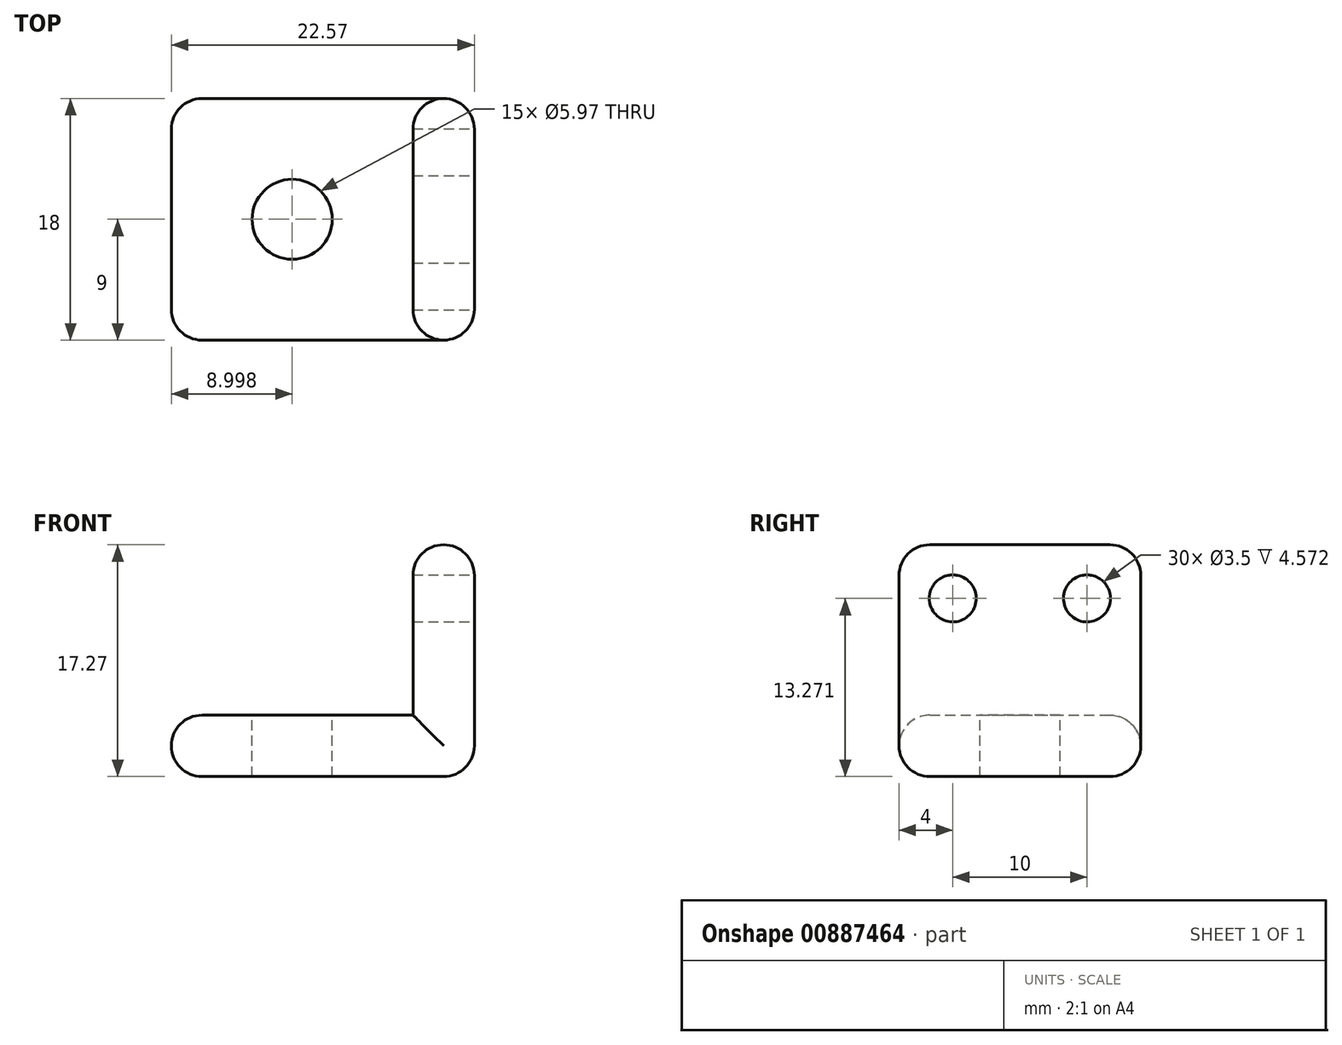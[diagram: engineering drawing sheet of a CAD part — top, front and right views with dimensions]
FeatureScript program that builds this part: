
annotation { "Feature Type Name" : "Feature", "Feature Type Description" : "" }
export const myFeature = defineFeature(function(context is Context, id is Id, definition is map)
    precondition{}
    {
        {
            var Q0;
            Q0=qCreatedBy(makeId("Front.planeOp"),FACE);
            var sketch = newSketch(context, id + "F0", { "sketchPlane" : qUnion([Q0])});
            skLineSegment(sketch, "E0.bottom", {"start": v(-12.02, -3.56) * mm, "end": v(5.98, -3.56) * mm});
            skLineSegment(sketch, "E0.top", {"start": v(-12.02, -8.13) * mm, "end": v(5.98, -8.13) * mm});
            skLineSegment(sketch, "E0.left", {"start": v(-12.02, -3.56) * mm, "end": v(-12.02, -8.13) * mm});
            skLineSegment(sketch, "E0.right", {"start": v(5.98, -3.56) * mm, "end": v(5.98, -8.13) * mm});
            skLineSegment(sketch, "E1.bottom", {"start": v(5.98, -8.13) * mm, "end": v(10.55, -8.13) * mm});
            skLineSegment(sketch, "E1.top", {"start": v(5.98, 9.14) * mm, "end": v(10.55, 9.14) * mm});
            skLineSegment(sketch, "E1.left", {"start": v(5.98, -8.13) * mm, "end": v(5.98, 9.14) * mm});
            skLineSegment(sketch, "E1.right", {"start": v(10.55, -8.13) * mm, "end": v(10.55, 9.14) * mm});
            skSolve(sketch);
        }
        {
            var Q0;
            {var subQ3=sQuery(id+"F0.wireOp",EDGE,"E1.bottom");Q0=makeQuery(id+"F0.imprint","IMPRINT",FACE,{"disambiguationData":[TD([[makeQuery(id+"F0.imprint","IMPRINT",EDGE,{"derivedFrom":subQ3}),1.0]])]});}
            var Q1;
            {var subQ0=sQuery(id+"F0.wireOp",EDGE,"E0.bottom");Q1=makeQuery(id+"F0.imprint","IMPRINT",FACE,{"disambiguationData":[TD([[makeQuery(id+"F0.imprint","IMPRINT",EDGE,{"derivedFrom":subQ0}),-1.0]])]});}
            extrude(context, id + "F1", {"entities" : qUnion([Q0, Q1]), "depth" : 18 * mm, "offsetDistance" : 25.4 * mm});
        }
        {
            var Q0;
            Q0=makeQuery(id+"F1.opExtrude","SWEPT_FACE",FACE,{"disambiguationData":[OSD([sQuery(id+"F0.wireOp",EDGE,"E0.bottom")])]});
            var sketch = newSketch(context, id + "F2", { "sketchPlane" : qUnion([Q0])});
            skCircle(sketch, "E2", {"center": v(-3.02, -9) * mm, "radius": 2.98 * mm});
            skPoint(sketch, "E2.centerSnap0", {"position": v(-12.02, -9) * mm});
            skSolve(sketch);
        }
        {
            var Q0;
            Q0=makeQuery(id+"F2.imprint","IMPRINT",FACE,{"disambiguationData":[TD([[makeQuery(id+"F2.imprint","IMPRINT",EDGE,{"derivedFrom":sQuery(id+"F2.wireOp",EDGE,"E2")}),1.0]])]});
            extrude(context, id + "F3", {"entities" : qUnion([Q0]), "operationType" : NewBodyOperationType.REMOVE, "oppositeDirection" : true, "depth" : 25.4 * mm, "offsetDistance" : 25.4 * mm});
        }
        {
            var Q0;
            Q0=makeQuery(id+"F1.opExtrude","SWEPT_FACE",FACE,{"disambiguationData":[OSD([sQuery(id+"F0.wireOp",EDGE,"E1.right")])]});
            var sketch = newSketch(context, id + "F4", { "sketchPlane" : qUnion([Q0])});
            skCircle(sketch, "E3", {"center": v(-14, 5.14) * mm, "radius": 1.75 * mm});
            skCircle(sketch, "E4", {"center": v(-4, 5.14) * mm, "radius": 1.75 * mm});
            skSolve(sketch);
        }
        {
            var Q0;
            Q0=makeQuery(id+"F4.imprint","IMPRINT",FACE,{"disambiguationData":[TD([[makeQuery(id+"F4.imprint","IMPRINT",EDGE,{"derivedFrom":sQuery(id+"F4.wireOp",EDGE,"E3")}),1.0]])]});
            var Q1;
            Q1=makeQuery(id+"F4.imprint","IMPRINT",FACE,{"disambiguationData":[TD([[makeQuery(id+"F4.imprint","IMPRINT",EDGE,{"derivedFrom":sQuery(id+"F4.wireOp",EDGE,"E4")}),1.0]])]});
            extrude(context, id + "F5", {"entities" : qUnion([Q0, Q1]), "operationType" : NewBodyOperationType.REMOVE, "oppositeDirection" : true, "depth" : 25.4 * mm, "offsetDistance" : 25.4 * mm});
        }
        {
            var Q0;
            Q0=makeQuery(id+"F1.opExtrude","CAP_EDGE",EDGE,{"disambiguationData":[OSD([sQuery(id+"F0.wireOp",EDGE,"E1.top")])],"isStart":false});
            var Q1;
            Q1=makeQuery(id+"F1.opExtrude","CAP_EDGE",EDGE,{"disambiguationData":[OSD([sQuery(id+"F0.wireOp",EDGE,"E1.top")])],"isStart":true});
            var Q2;
            Q2=makeQuery(id+"F1.opExtrude","CAP_EDGE",EDGE,{"disambiguationData":[OSD([sQuery(id+"F0.wireOp",EDGE,"E0.left")])],"isStart":false});
            var Q3;
            Q3=makeQuery(id+"F1.opExtrude","CAP_EDGE",EDGE,{"disambiguationData":[OSD([sQuery(id+"F0.wireOp",EDGE,"E0.left")])],"isStart":true});
            var Q4;
            Q4=makeQuery(id+"F1.opExtrude","CAP_FACE",FACE,{"disambiguationData":[OSD([sQuery(id+"F0.wireOp",EDGE,"E0.bottom"),sQuery(id+"F0.wireOp",EDGE,"E0.top"),sQuery(id+"F0.wireOp",EDGE,"E0.left"),sQuery(id+"F0.wireOp",EDGE,"E1.bottom"),sQuery(id+"F0.wireOp",EDGE,"E1.top"),sQuery(id+"F0.wireOp",EDGE,"E1.left"),sQuery(id+"F0.wireOp",EDGE,"E1.right")])],"isStart":false});
            var Q5;
            Q5=makeQuery(id+"F1.opExtrude","CAP_FACE",FACE,{"disambiguationData":[OSD([sQuery(id+"F0.wireOp",EDGE,"E0.bottom"),sQuery(id+"F0.wireOp",EDGE,"E0.top"),sQuery(id+"F0.wireOp",EDGE,"E0.left"),sQuery(id+"F0.wireOp",EDGE,"E1.bottom"),sQuery(id+"F0.wireOp",EDGE,"E1.top"),sQuery(id+"F0.wireOp",EDGE,"E1.left"),sQuery(id+"F0.wireOp",EDGE,"E1.right")])],"isStart":true});
            var Q6;
            Q6=makeQuery(id+"F1.opExtrude","SWEPT_FACE",FACE,{"disambiguationData":[OSD([sQuery(id+"F0.wireOp",EDGE,"E0.left")])]});
            var Q7;
            Q7=makeQuery(id+"F1.opExtrude","SWEPT_EDGE",EDGE,{"disambiguationData":[OSD([sQuery(id+"F0.wireOp",EDGE,"E1.bottom"),sQuery(id+"F0.wireOp",EDGE,"E1.right")])]});
            var Q8;
            Q8=makeQuery(id+"F1.opExtrude","SWEPT_FACE",FACE,{"disambiguationData":[OSD([sQuery(id+"F0.wireOp",EDGE,"E1.top")])]});
            fillet(context, id + "F6", {"entities" : qUnion([Q0, Q1, Q2, Q3, Q4, Q5, Q6, Q7, Q8]), "radius" : 2.3 * mm, "tangentPropagation" : true, "allowEdgeOverflow" : false});
        }
    });
